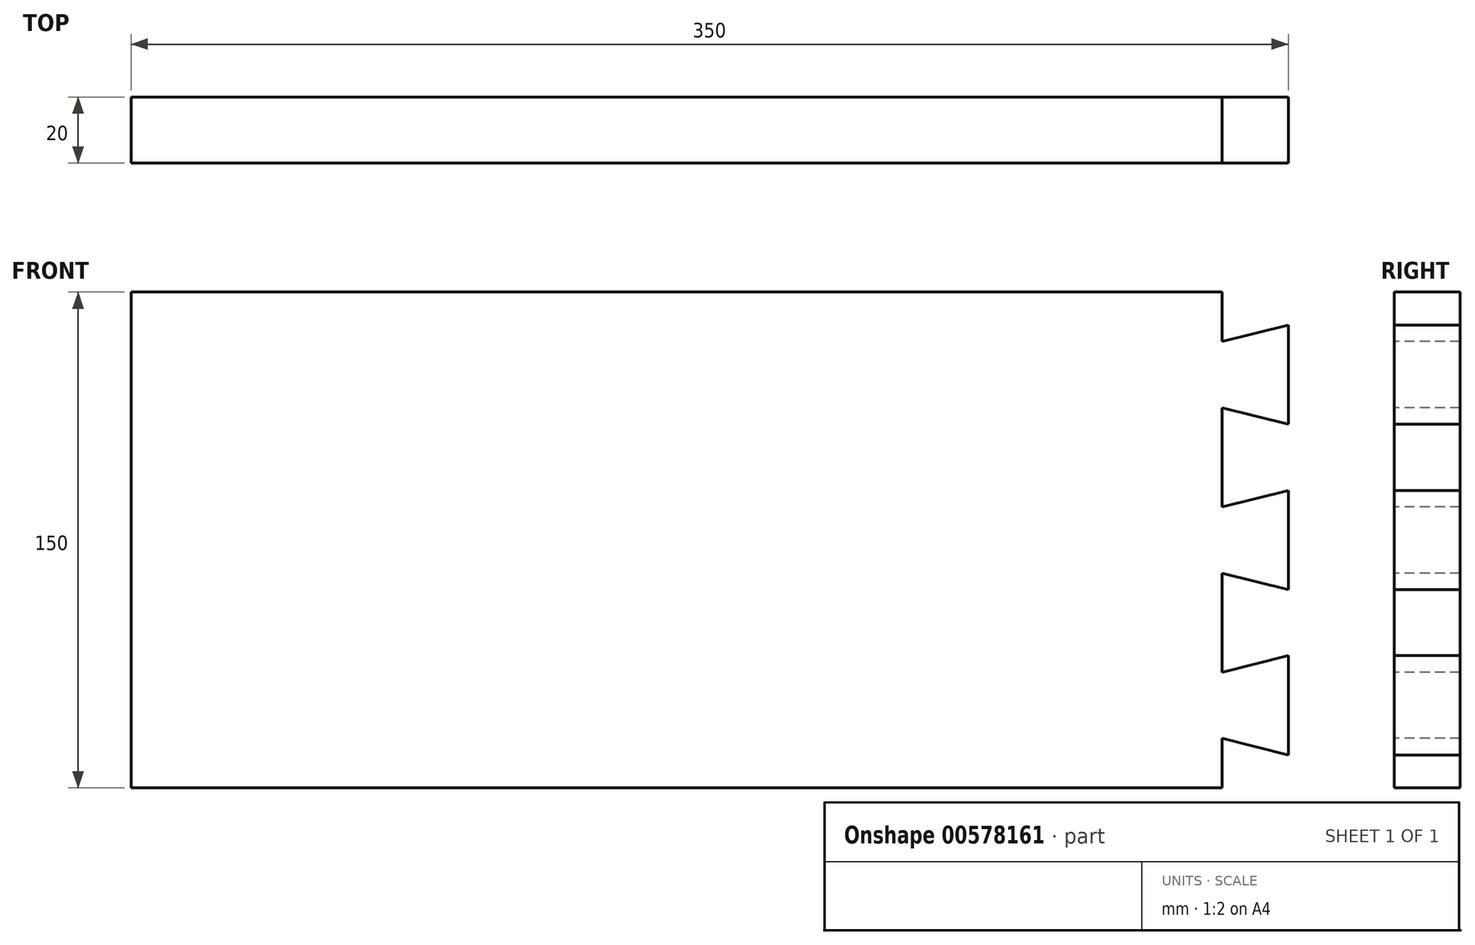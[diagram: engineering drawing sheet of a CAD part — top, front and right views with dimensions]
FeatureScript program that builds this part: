
annotation { "Feature Type Name" : "Feature", "Feature Type Description" : "" }
export const myFeature = defineFeature(function(context is Context, id is Id, definition is map)
    precondition{}
    {
        {
            var Q0;
            Q0=qCreatedBy(makeId("Front.planeOp"),FACE);
            var sketch = newSketch(context, id + "F0", { "sketchPlane" : qUnion([Q0])});
            skLineSegment(sketch, "E0.bottom", {"start": v(-167.06, 115) * mm, "end": v(162.94, 115) * mm});
            skLineSegment(sketch, "E0.top", {"start": v(-167.06, -35) * mm, "end": v(162.94, -35) * mm});
            skLineSegment(sketch, "E0.left", {"start": v(-187.06, 105) * mm, "end": v(-187.06, 75) * mm});
            skLineSegment(sketch, "E0.right", {"start": v(162.94, 115) * mm, "end": v(162.94, -35) * mm});
            skLineSegment(sketch, "E1", {"start": v(-167.06, 115) * mm, "end": v(-167.06, 100) * mm});
            skLineSegment(sketch, "E2", {"start": v(-187.06, 40) * mm, "end": v(-187.06, 55) * mm});
            skLineSegment(sketch, "E3", {"start": v(-187.06, 55) * mm, "end": v(-187.06, 40) * mm});
            skLineSegment(sketch, "E4", {"start": v(-187.06, 40) * mm, "end": v(-187.06, 25) * mm});
            skLineSegment(sketch, "E5", {"start": v(-187.06, 25) * mm, "end": v(-167.06, 30) * mm});
            skLineSegment(sketch, "E6", {"start": v(-167.06, 50) * mm, "end": v(-187.06, 55) * mm});
            skLineSegment(sketch, "E7", {"start": v(-167.06, 30) * mm, "end": v(-167.06, 0) * mm});
            skLineSegment(sketch, "E8", {"start": v(-167.06, 0) * mm, "end": v(-187.06, 5) * mm});
            skLineSegment(sketch, "E9", {"start": v(-187.06, 5) * mm, "end": v(-187.06, -25) * mm});
            skLineSegment(sketch, "E10", {"start": v(-187.06, -25) * mm, "end": v(-167.06, -20) * mm});
            skLineSegment(sketch, "E11", {"start": v(-167.06, 50) * mm, "end": v(-167.06, 80) * mm});
            skLineSegment(sketch, "E12", {"start": v(-167.06, 80) * mm, "end": v(-187.06, 75) * mm});
            skLineSegment(sketch, "E13", {"start": v(-187.06, 75) * mm, "end": v(-187.06, 105) * mm});
            skLineSegment(sketch, "E14", {"start": v(-187.06, 105) * mm, "end": v(-167.06, 100) * mm});
            skPoint(sketch, "E15.orphan", {"position": v(-187.06, 115) * mm});
            skLineSegment(sketch, "E16.trimOffspring", {"start": v(-187.06, 55) * mm, "end": v(-187.06, 25) * mm});
            skPoint(sketch, "E17.orphan", {"position": v(-187.06, -35) * mm});
            skLineSegment(sketch, "E18.trimOffspring", {"start": v(-167.06, 80) * mm, "end": v(-167.06, 50) * mm});
            skPoint(sketch, "E19.end.orphan", {"position": v(-167.06, 40) * mm});
            skLineSegment(sketch, "E20.trimOffspring", {"start": v(-167.06, -20) * mm, "end": v(-167.06, -35) * mm});
            skSolve(sketch);
        }
        {
            var Q0;
            Q0=makeQuery(id+"F0.imprint","IMPRINT",FACE,{"disambiguationData":[TD([[makeQuery(id+"F0.imprint","IMPRINT",EDGE,{"derivedFrom":sQuery(id+"F0.wireOp",EDGE,"E0.bottom")}),-1.0]])]});
            extrude(context, id + "F1", {"entities" : qUnion([Q0]), "depth" : 20 * mm, "offsetDistance" : 25 * mm});
        }
        {
            var Q0;
            Q0=makeQuery(id+"F1.opExtrude","SWEPT_BODY",BODY,{"disambiguationData":[OSD([sQuery(id+"F0.wireOp",EDGE,"E0.bottom"),sQuery(id+"F0.wireOp",EDGE,"E0.top"),sQuery(id+"F0.wireOp",EDGE,"E0.right"),sQuery(id+"F0.wireOp",EDGE,"E1"),sQuery(id+"F0.wireOp",EDGE,"E5"),sQuery(id+"F0.wireOp",EDGE,"E6"),sQuery(id+"F0.wireOp",EDGE,"E8"),sQuery(id+"F0.wireOp",EDGE,"E10"),sQuery(id+"F0.wireOp",EDGE,"E12"),sQuery(id+"F0.wireOp",EDGE,"E13"),sQuery(id+"F0.wireOp",EDGE,"E14"),sQuery(id+"F0.wireOp",EDGE,"E16.trimOffspring"),sQuery(id+"F0.wireOp",EDGE,"E9"),sQuery(id+"F0.wireOp",EDGE,"E18.trimOffspring"),sQuery(id+"F0.wireOp",EDGE,"E7"),sQuery(id+"F0.wireOp",EDGE,"E20.trimOffspring")])]});
            var Q1;
            Q1=makeQuery(id+"F1.opExtrude","CAP_EDGE",EDGE,{"disambiguationData":[OSD([sQuery(id+"F0.wireOp",EDGE,"E0.right")])],"isStart":false});
            transform(context, id + "F2", {"entities" : qUnion([Q0]), "transformType" : TransformType.ROTATION, "transformAxis" : qUnion([Q1]), "angle" : 180 * degree, "makeCopy" : false});
        }
    });
